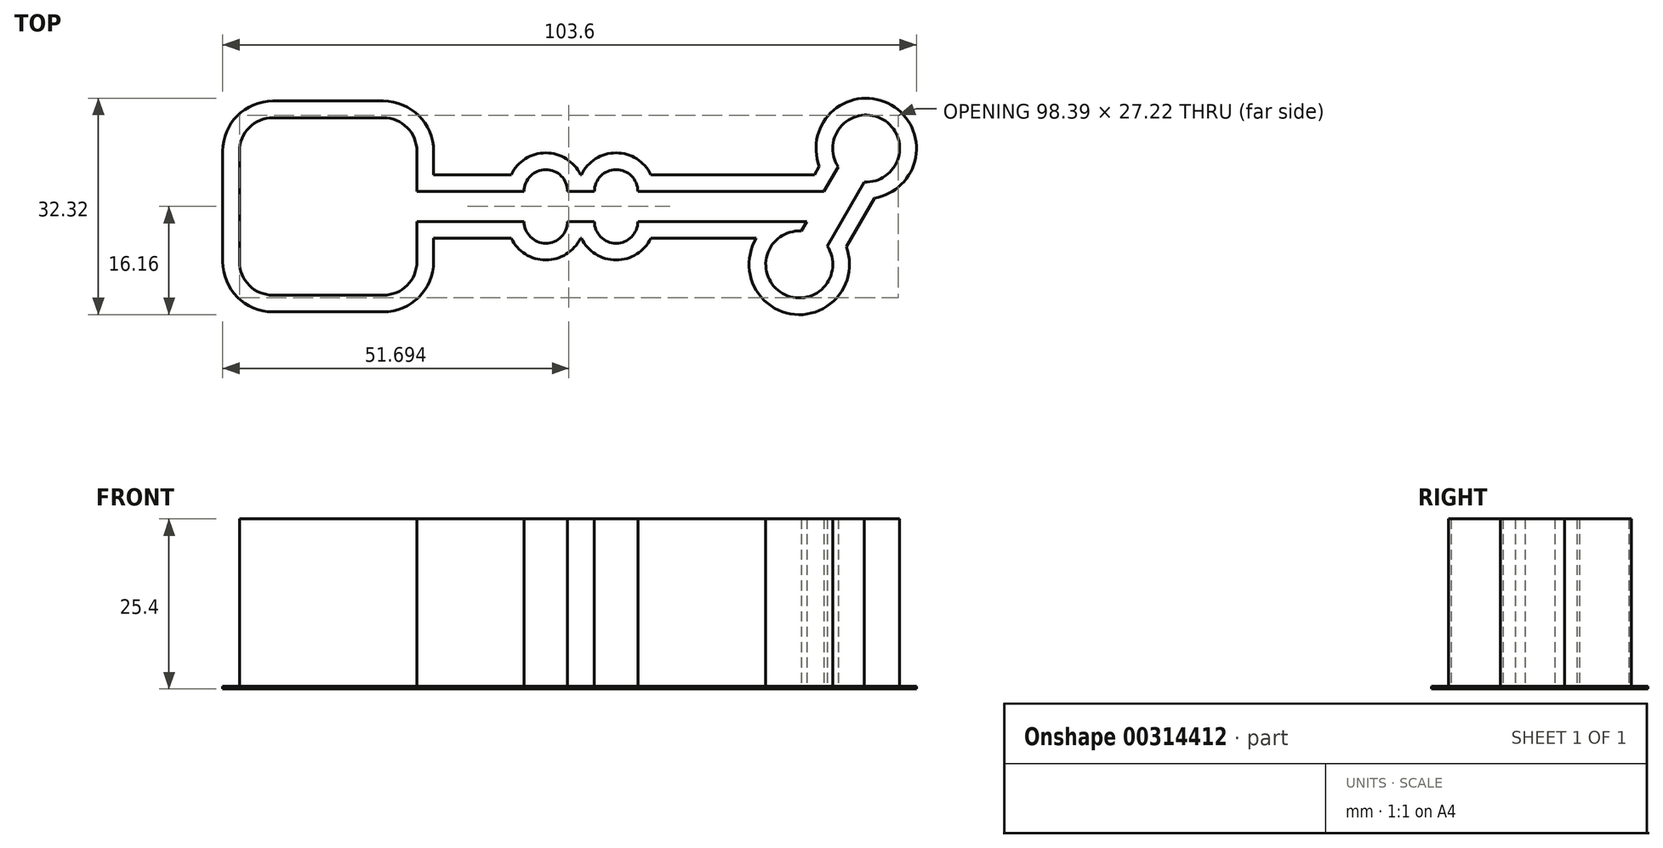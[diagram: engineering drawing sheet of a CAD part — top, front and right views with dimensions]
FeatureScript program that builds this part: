
annotation { "Feature Type Name" : "Feature", "Feature Type Description" : "" }
export const myFeature = defineFeature(function(context is Context, id is Id, definition is map)
    precondition{}
    {
        {
            var Q0;
            Q0=qCreatedBy(makeId("Top.planeOp"),FACE);
            var sketch = newSketch(context, id + "F0", { "sketchPlane" : qUnion([Q0])});
            skLineSegment(sketch, "E0.bottom", {"start": v(8.25, -13.25) * mm, "end": v(-8.25, -13.25) * mm});
            skLineSegment(sketch, "E0.top", {"start": v(8.25, 13.25) * mm, "end": v(-8.25, 13.25) * mm});
            skLineSegment(sketch, "E0.left", {"start": v(13.25, -8.25) * mm, "end": v(13.25, -2.25) * mm});
            skLineSegment(sketch, "E0.right", {"start": v(-13.25, -8.25) * mm, "end": v(-13.25, 8.25) * mm});
            skPoint(sketch, "E0.middle", {"position": v(0, 0) * mm});
            skCircle(sketch, "E1", {"center": v(0, 0) * mm, "radius": 4.5 * mm});
            skLineSegment(sketch, "E2", {"start": v(-26.75, 0) * mm, "end": v(92.45, 0) * mm, "construction": true});
            skPoint(sketch, "E2.startSnap0", {"position": v(-13.25, 0) * mm});
            skPoint(sketch, "E2.endSnap0", {"position": v(-13.25, 0) * mm});
            skLineSegment(sketch, "E3", {"start": v(-13.25, 4.5) * mm, "end": v(13.25, 4.5) * mm});
            skLineSegment(sketch, "E4", {"start": v(-4.5, 13.25) * mm, "end": v(-4.5, 0) * mm});
            skLineSegment(sketch, "E5", {"start": v(4.5, 13.25) * mm, "end": v(4.5, 0) * mm});
            skLineSegment(sketch, "E6.MirrorCS", {"start": v(4.5, -13.25) * mm, "end": v(4.5, 0) * mm});
            skLineSegment(sketch, "E7.MirrorCS", {"start": v(-4.5, -13.25) * mm, "end": v(-4.5, 0) * mm});
            skLineSegment(sketch, "E8.MirrorCS", {"start": v(-13.25, -4.5) * mm, "end": v(13.25, -4.5) * mm});
            skPoint(sketch, "E9.visualSharp", {"position": v(13.25, 13.25) * mm});
            skArc(sketch, "E9.filletArc", {"start": v(13.25, 8.25) * mm, "mid": v(11.79, 11.79) * mm, "end": v(8.25, 13.25) * mm});
            skPoint(sketch, "E10.visualSharp", {"position": v(13.25, -13.25) * mm});
            skArc(sketch, "E10.filletArc", {"start": v(8.25, -13.25) * mm, "mid": v(11.79, -11.79) * mm, "end": v(13.25, -8.25) * mm});
            skPoint(sketch, "E11.visualSharp", {"position": v(-13.25, -13.25) * mm});
            skArc(sketch, "E11.filletArc", {"start": v(-13.25, -8.25) * mm, "mid": v(-11.79, -11.79) * mm, "end": v(-8.25, -13.25) * mm});
            skPoint(sketch, "E12.visualSharp", {"position": v(-13.25, 13.25) * mm});
            skArc(sketch, "E12.filletArc", {"start": v(-8.25, 13.25) * mm, "mid": v(-11.79, 11.79) * mm, "end": v(-13.25, 8.25) * mm});
            skLineSegment(sketch, "E13", {"start": v(13.25, 2.25) * mm, "end": v(29.25, 2.25) * mm});
            skLineSegment(sketch, "E14.bottom", {"start": v(29.25, 2.25) * mm, "end": v(35.75, 2.25) * mm});
            skLineSegment(sketch, "E14.top", {"start": v(29.25, -2.25) * mm, "end": v(35.75, -2.25) * mm});
            skLineSegment(sketch, "E14.left", {"start": v(29.25, 2.25) * mm, "end": v(29.25, -2.25) * mm});
            skLineSegment(sketch, "E14.right", {"start": v(35.75, 2.25) * mm, "end": v(35.75, -2.25) * mm});
            skArc(sketch, "E15", {"start": v(29.25, 2.25) * mm, "mid": v(32.5, 5.5) * mm, "end": v(35.75, 2.25) * mm});
            skLineSegment(sketch, "E16", {"start": v(35.75, 2.25) * mm, "end": v(37.75, 2.25) * mm});
            skLineSegment(sketch, "E17", {"start": v(37.75, 3.76) * mm, "end": v(37.75, -18.1) * mm, "construction": true});
            skLineSegment(sketch, "E18", {"start": v(37.75, -18.1) * mm, "end": v(37.75, -6.16) * mm});
            skLineSegment(sketch, "E19.MirrorCS", {"start": v(13.25, -2.25) * mm, "end": v(13.25, -2.25) * mm});
            skArc(sketch, "E20.MirrorCS", {"start": v(29.25, -2.25) * mm, "mid": v(32.5, -5.5) * mm, "end": v(35.75, -2.25) * mm});
            skLineSegment(sketch, "E21.MirrorCS", {"start": v(35.75, -2.25) * mm, "end": v(37.75, -2.25) * mm});
            skLineSegment(sketch, "E22.MirrorCS", {"start": v(39.75, 2.25) * mm, "end": v(37.75, 2.25) * mm});
            skLineSegment(sketch, "E23.MirrorCS", {"start": v(39.75, -2.25) * mm, "end": v(37.75, -2.25) * mm});
            skArc(sketch, "E24.MirrorCS", {"start": v(46.25, 2.25) * mm, "mid": v(43, 5.5) * mm, "end": v(39.75, 2.25) * mm});
            skLineSegment(sketch, "E25.MirrorCS", {"start": v(46.25, 2.25) * mm, "end": v(39.75, 2.25) * mm});
            skArc(sketch, "E26.MirrorCS", {"start": v(46.25, -2.25) * mm, "mid": v(43, -5.5) * mm, "end": v(39.75, -2.25) * mm});
            skLineSegment(sketch, "E27.MirrorCS", {"start": v(46.25, -2.25) * mm, "end": v(39.75, -2.25) * mm});
            skLineSegment(sketch, "E28.MirrorCS", {"start": v(46.25, 2.25) * mm, "end": v(46.25, -2.25) * mm});
            skLineSegment(sketch, "E29.MirrorCS", {"start": v(39.75, 2.25) * mm, "end": v(39.75, -2.25) * mm});
            skLineSegment(sketch, "E30", {"start": v(46.25, 2.25) * mm, "end": v(74.05, 2.25) * mm});
            skLineSegment(sketch, "E31.MirrorCS", {"start": v(46.25, -2.25) * mm, "end": v(71.45, -2.25) * mm});
            skLineSegment(sketch, "E32", {"start": v(80.35, 8.66) * mm, "end": v(70.35, -8.66) * mm, "construction": true});
            skPoint(sketch, "E33", {"position": v(75.35, 0) * mm});
            skLineSegment(sketch, "E34", {"start": v(76.17, 5.92) * mm, "end": v(76.17, 5.92) * mm});
            skLineSegment(sketch, "E35.0", {"start": v(80.06, 3.67) * mm, "end": v(74.53, -5.92) * mm});
            skPoint(sketch, "E36", {"position": v(72.75, 0) * mm});
            skPoint(sketch, "E37.orphan", {"position": v(72.75, -2.25) * mm});
            skPoint(sketch, "E38.orphan", {"position": v(72.75, 2.25) * mm});
            skLineSegment(sketch, "E39", {"start": v(76.17, 5.92) * mm, "end": v(74.05, 2.25) * mm});
            skArc(sketch, "E40", {"start": v(76.17, 5.92) * mm, "mid": v(77.85, 4.33) * mm, "end": v(80.06, 3.67) * mm});
            skArc(sketch, "E41", {"start": v(80.06, 3.67) * mm, "mid": v(82.85, 13) * mm, "end": v(76.17, 5.92) * mm});
            skLineSegment(sketch, "E42", {"start": v(70.63, -3.67) * mm, "end": v(70.63, -3.67) * mm});
            skLineSegment(sketch, "E43", {"start": v(71.45, -2.25) * mm, "end": v(70.63, -3.67) * mm});
            skLineSegment(sketch, "E44", {"start": v(74.05, 2.25) * mm, "end": v(71.45, -2.25) * mm});
            skArc(sketch, "E45", {"start": v(70.63, -3.67) * mm, "mid": v(67.85, -13) * mm, "end": v(74.53, -5.92) * mm});
            skArc(sketch, "E46", {"start": v(74.53, -5.92) * mm, "mid": v(72.85, -4.33) * mm, "end": v(70.63, -3.67) * mm});
            skLineSegment(sketch, "E47", {"start": v(13.25, -2.25) * mm, "end": v(29.25, -2.25) * mm});
            skLineSegment(sketch, "E48", {"start": v(13.25, 2.25) * mm, "end": v(13.25, 8.25) * mm});
            skLineSegment(sketch, "E49", {"start": v(13.25, -2.25) * mm, "end": v(13.25, 2.25) * mm});
            skLineSegment(sketch, "E50.0", {"start": v(15.75, 4.75) * mm, "end": v(15.75, 8.25) * mm});
            skArc(sketch, "E50.1", {"start": v(15.75, 8.25) * mm, "mid": v(13.55, 13.55) * mm, "end": v(8.25, 15.75) * mm});
            skLineSegment(sketch, "E50.2", {"start": v(48.18, -4.75) * mm, "end": v(63.95, -4.75) * mm});
            skArc(sketch, "E50.3", {"start": v(63.95, -4.75) * mm, "mid": v(69.65, -16.13) * mm, "end": v(77.36, -6) * mm});
            skLineSegment(sketch, "E50.4", {"start": v(81.56, 1.26) * mm, "end": v(77.36, -6) * mm});
            skArc(sketch, "E50.5", {"start": v(81.56, 1.26) * mm, "mid": v(84.1, 15.16) * mm, "end": v(73.33, 6) * mm});
            skLineSegment(sketch, "E50.6", {"start": v(73.33, 6) * mm, "end": v(72.6, 4.75) * mm});
            skLineSegment(sketch, "E50.7", {"start": v(48.18, 4.75) * mm, "end": v(72.6, 4.75) * mm});
            skArc(sketch, "E50.8", {"start": v(27.32, 4.75) * mm, "mid": v(32.5, 8) * mm, "end": v(37.68, 4.75) * mm});
            skLineSegment(sketch, "E50.9", {"start": v(37.68, 4.75) * mm, "end": v(37.75, 4.75) * mm});
            skLineSegment(sketch, "E50.10", {"start": v(37.82, 4.75) * mm, "end": v(37.75, 4.75) * mm});
            skArc(sketch, "E50.11", {"start": v(48.18, 4.75) * mm, "mid": v(43, 8) * mm, "end": v(37.82, 4.75) * mm});
            skArc(sketch, "E50.12", {"start": v(48.18, -4.75) * mm, "mid": v(43, -8) * mm, "end": v(37.82, -4.75) * mm});
            skLineSegment(sketch, "E50.13", {"start": v(37.82, -4.75) * mm, "end": v(37.75, -4.75) * mm});
            skLineSegment(sketch, "E50.14", {"start": v(15.75, 4.75) * mm, "end": v(27.32, 4.75) * mm});
            skLineSegment(sketch, "E50.15", {"start": v(37.68, -4.75) * mm, "end": v(37.75, -4.75) * mm});
            skArc(sketch, "E50.16", {"start": v(27.32, -4.75) * mm, "mid": v(32.5, -8) * mm, "end": v(37.68, -4.75) * mm});
            skLineSegment(sketch, "E50.17", {"start": v(15.75, -4.75) * mm, "end": v(27.32, -4.75) * mm});
            skLineSegment(sketch, "E50.18", {"start": v(15.75, -8.25) * mm, "end": v(15.75, -4.75) * mm});
            skArc(sketch, "E50.19", {"start": v(8.25, -15.75) * mm, "mid": v(13.55, -13.55) * mm, "end": v(15.75, -8.25) * mm});
            skLineSegment(sketch, "E50.20", {"start": v(8.25, -15.75) * mm, "end": v(-8.25, -15.75) * mm});
            skArc(sketch, "E50.21", {"start": v(-15.75, -8.25) * mm, "mid": v(-13.55, -13.55) * mm, "end": v(-8.25, -15.75) * mm});
            skLineSegment(sketch, "E50.22", {"start": v(-15.75, -8.25) * mm, "end": v(-15.75, 8.25) * mm});
            skArc(sketch, "E50.23", {"start": v(-8.25, 15.75) * mm, "mid": v(-13.55, 13.55) * mm, "end": v(-15.75, 8.25) * mm});
            skLineSegment(sketch, "E50.24", {"start": v(8.25, 15.75) * mm, "end": v(-8.25, 15.75) * mm});
            skSolve(sketch);
        }
        {
            var Q0;
            Q0 = qSketchRegion(id + "F0", true);
            extrude(context, id + "F1", {"entities" : qUnion([Q0]), "depth" : 0.4 * mm});
        }
        {
            var Q0;
            Q0=makeQuery(id+"F1.opExtrude","CAP_FACE",FACE,{"disambiguationData":[OSD([sQuery(id+"F0.wireOp",EDGE,"E0.bottom"),sQuery(id+"F0.wireOp",EDGE,"E0.top"),sQuery(id+"F0.wireOp",EDGE,"E0.left"),sQuery(id+"F0.wireOp",EDGE,"E0.right"),sQuery(id+"F0.wireOp",EDGE,"E9.filletArc"),sQuery(id+"F0.wireOp",EDGE,"E10.filletArc"),sQuery(id+"F0.wireOp",EDGE,"E11.filletArc"),sQuery(id+"F0.wireOp",EDGE,"E12.filletArc"),sQuery(id+"F0.wireOp",EDGE,"E13"),sQuery(id+"F0.wireOp",EDGE,"E15"),sQuery(id+"F0.wireOp",EDGE,"E16"),sQuery(id+"F0.wireOp",EDGE,"E20.MirrorCS"),sQuery(id+"F0.wireOp",EDGE,"E21.MirrorCS"),sQuery(id+"F0.wireOp",EDGE,"E22.MirrorCS"),sQuery(id+"F0.wireOp",EDGE,"E23.MirrorCS"),sQuery(id+"F0.wireOp",EDGE,"E24.MirrorCS"),sQuery(id+"F0.wireOp",EDGE,"E26.MirrorCS"),sQuery(id+"F0.wireOp",EDGE,"E30"),sQuery(id+"F0.wireOp",EDGE,"E31.MirrorCS"),sQuery(id+"F0.wireOp",EDGE,"E35.0"),sQuery(id+"F0.wireOp",EDGE,"E39"),sQuery(id+"F0.wireOp",EDGE,"E41"),sQuery(id+"F0.wireOp",EDGE,"E43"),sQuery(id+"F0.wireOp",EDGE,"E45"),sQuery(id+"F0.wireOp",EDGE,"E47"),sQuery(id+"F0.wireOp",EDGE,"E48"),sQuery(id+"F0.wireOp",EDGE,"E50.0"),sQuery(id+"F0.wireOp",EDGE,"E50.1"),sQuery(id+"F0.wireOp",EDGE,"E50.2"),sQuery(id+"F0.wireOp",EDGE,"E50.3"),sQuery(id+"F0.wireOp",EDGE,"E50.4"),sQuery(id+"F0.wireOp",EDGE,"E50.5"),sQuery(id+"F0.wireOp",EDGE,"E50.6"),sQuery(id+"F0.wireOp",EDGE,"E50.7"),sQuery(id+"F0.wireOp",EDGE,"E50.8"),sQuery(id+"F0.wireOp",EDGE,"E50.9"),sQuery(id+"F0.wireOp",EDGE,"E50.10"),sQuery(id+"F0.wireOp",EDGE,"E50.11"),sQuery(id+"F0.wireOp",EDGE,"E50.12"),sQuery(id+"F0.wireOp",EDGE,"E50.13"),sQuery(id+"F0.wireOp",EDGE,"E50.14"),sQuery(id+"F0.wireOp",EDGE,"E50.15"),sQuery(id+"F0.wireOp",EDGE,"E50.16"),sQuery(id+"F0.wireOp",EDGE,"E50.17"),sQuery(id+"F0.wireOp",EDGE,"E50.18"),sQuery(id+"F0.wireOp",EDGE,"E50.19"),sQuery(id+"F0.wireOp",EDGE,"E50.20"),sQuery(id+"F0.wireOp",EDGE,"E50.21"),sQuery(id+"F0.wireOp",EDGE,"E50.22"),sQuery(id+"F0.wireOp",EDGE,"E50.23"),sQuery(id+"F0.wireOp",EDGE,"E50.24")])],"isStart":false});
            var sketch = newSketch(context, id + "F2", { "sketchPlane" : qUnion([Q0])});
            skSolve(sketch);
        }
        {
            var Q0;
            Q0=makeQuery(id+"F2.imprint","IMPRINT",FACE,{"disambiguationData":[TD([[makeQuery(id+"F2.imprint","IMPRINT",EDGE,{"derivedFrom":makeQuery(id+"F1.opExtrude","CAP_EDGE",EDGE,{"disambiguationData":[OSD([sQuery(id+"F0.wireOp",EDGE,"E0.bottom")])],"isStart":false})}),-1.0]])]});
            extrude(context, id + "F3", {"entities" : qUnion([Q0]), "depth" : 25 * mm});
        }
    });
